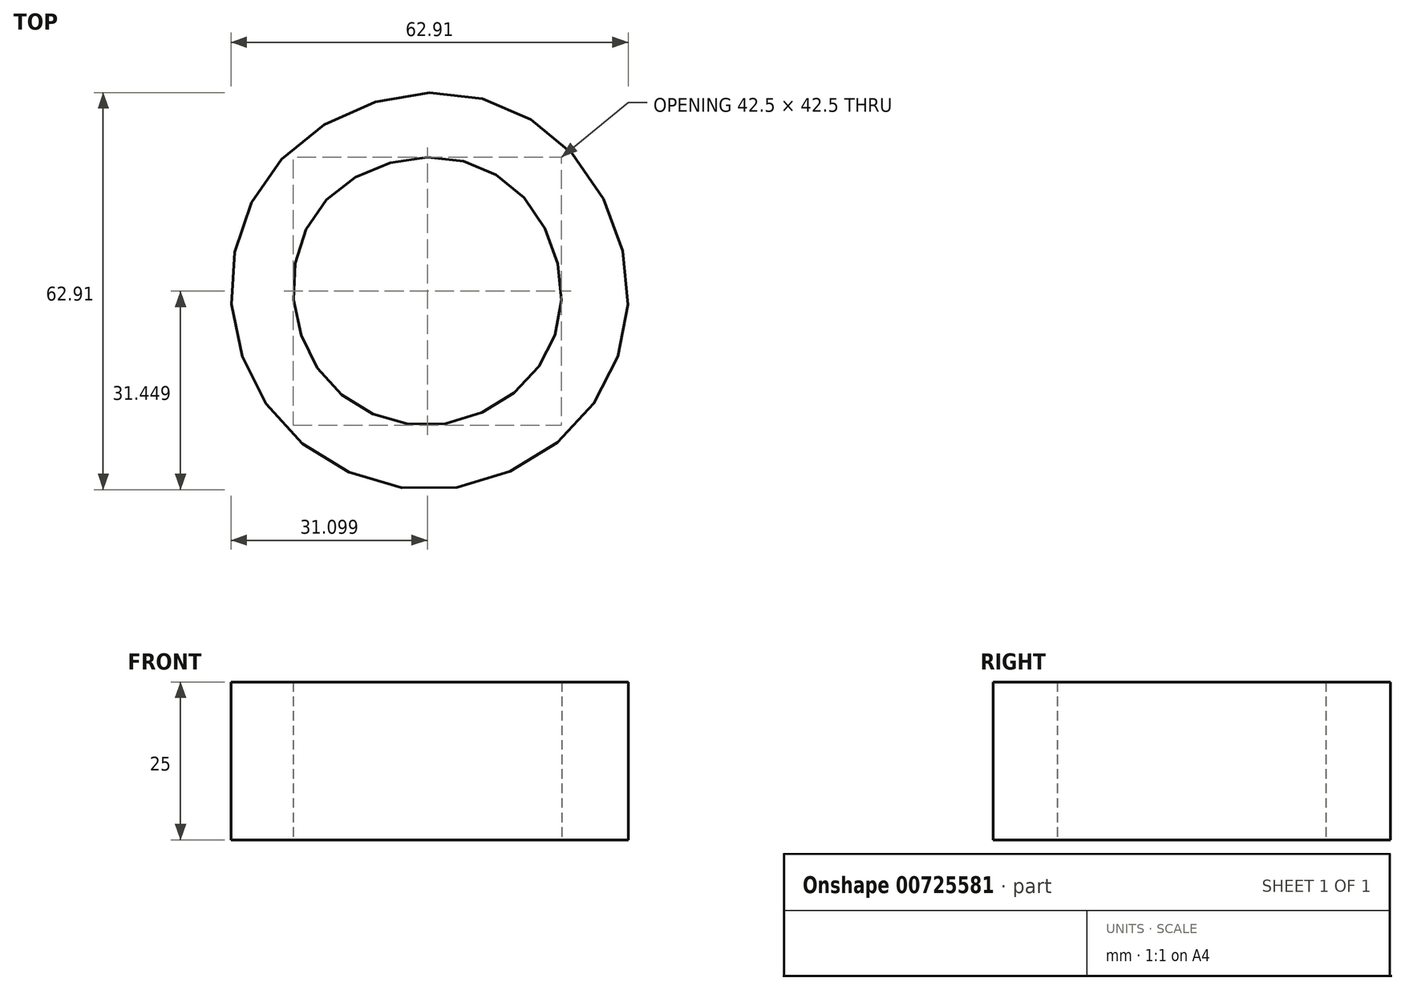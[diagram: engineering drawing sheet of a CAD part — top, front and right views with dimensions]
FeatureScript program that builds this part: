
annotation { "Feature Type Name" : "Feature", "Feature Type Description" : "" }
export const myFeature = defineFeature(function(context is Context, id is Id, definition is map)
    precondition{}
    {
        {
            var Q0;
            Q0=qCreatedBy(makeId("Top.planeOp"),FACE);
            var sketch = newSketch(context, id + "F0", { "sketchPlane" : qUnion([Q0])});
            skFitSpline(sketch, "E0", {"points": [v(0, 31.45) * mm, v(21.5, 22.9) * mm, v(31.45, 0) * mm, v(23, -21.4) * mm, v(0, -31.45) * mm, v(-22.8, -21.7) * mm, v(-31.45, 0) * mm, v(-23.15, 21.25) * mm, v(0, 31.45) * mm]});
            skSolve(sketch);
        }
        {
            var Q0;
            Q0 = qSketchRegion(id + "F0", true);
            extrude(context, id + "F1", {"entities" : qUnion([Q0]), "oppositeDirection" : true, "depth" : 25 * mm, "offsetDistance" : 25 * mm});
        }
        {
            var Q0;
            Q0=makeQuery(id+"F1.opExtrude","CAP_FACE",FACE,{"disambiguationData":[OSD([sQuery(id+"F0.wireOp",EDGE,"E0")])],"isStart":true});
            var sketch = newSketch(context, id + "F2", { "sketchPlane" : qUnion([Q0])});
            skFitSpline(sketch, "E1", {"points": [v(-0.35, 21.25) * mm, v(14.2, 15.6) * mm, v(20.9, 0) * mm, v(15.35, -14.3) * mm, v(-0.35, -21.25) * mm, v(-15.5, -14.95) * mm, v(-21.6, 0) * mm, v(-16.15, 14.7) * mm, v(-0.35, 21.25) * mm]});
            skSolve(sketch);
        }
        {
            var Q0;
            Q0 = qSketchRegion(id + "F2", true);
            extrude(context, id + "F3", {"entities" : qUnion([Q0]), "operationType" : NewBodyOperationType.REMOVE, "endBound" : BoundingType.THROUGH_ALL, "oppositeDirection" : true, "depth" : 25 * mm, "offsetDistance" : 25 * mm});
        }
    });
